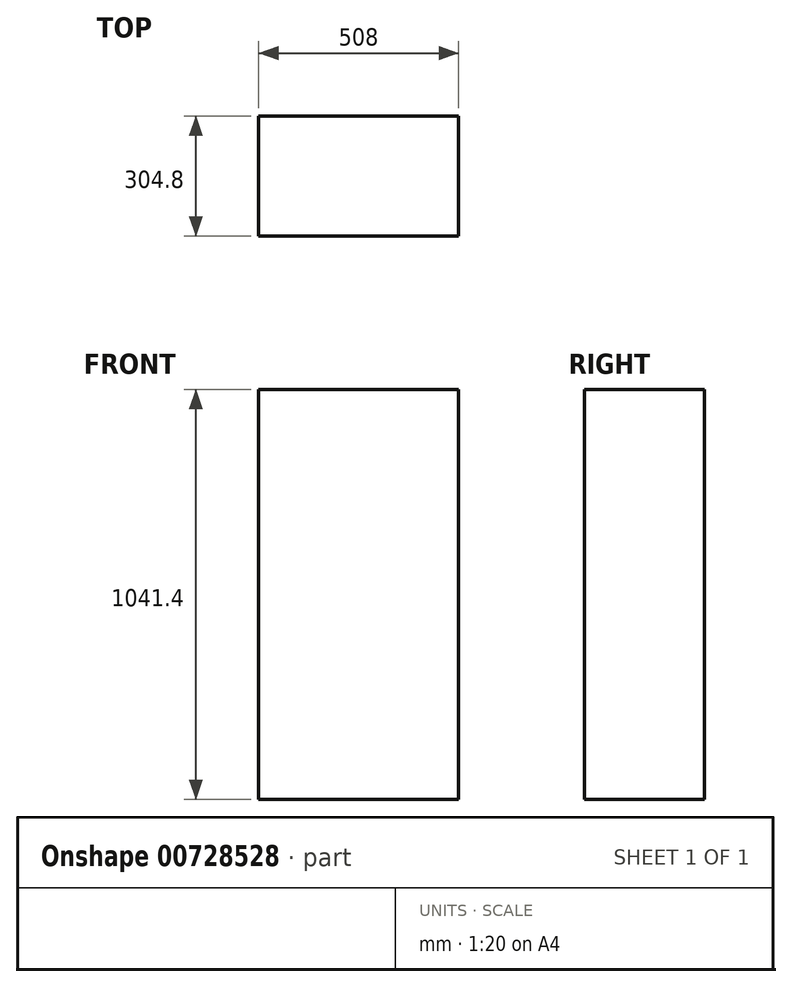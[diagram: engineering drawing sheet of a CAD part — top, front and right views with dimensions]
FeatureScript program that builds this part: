
annotation { "Feature Type Name" : "Feature", "Feature Type Description" : "" }
export const myFeature = defineFeature(function(context is Context, id is Id, definition is map)
    precondition{}
    {
        {
            var Q0;
            Q0=qCreatedBy(makeId("Top.planeOp"),FACE);
            var sketch = newSketch(context, id + "F0", { "sketchPlane" : qUnion([Q0])});
            skLineSegment(sketch, "E0.bottom", {"start": v(254, 152.4) * mm, "end": v(-254, 152.4) * mm});
            skLineSegment(sketch, "E0.top", {"start": v(254, -152.4) * mm, "end": v(-254, -152.4) * mm});
            skLineSegment(sketch, "E0.left", {"start": v(254, 152.4) * mm, "end": v(254, -152.4) * mm});
            skLineSegment(sketch, "E0.right", {"start": v(-254, 152.4) * mm, "end": v(-254, -152.4) * mm});
            skPoint(sketch, "E0.middle", {"position": v(0, 0) * mm});
            skSolve(sketch);
        }
        {
            var Q0;
            Q0 = qSketchRegion(id + "F0", true);
            extrude(context, id + "F1", {"entities" : qUnion([Q0]), "depth" : 1041.4 * mm, "offsetDistance" : 25.4 * mm});
        }
    });
